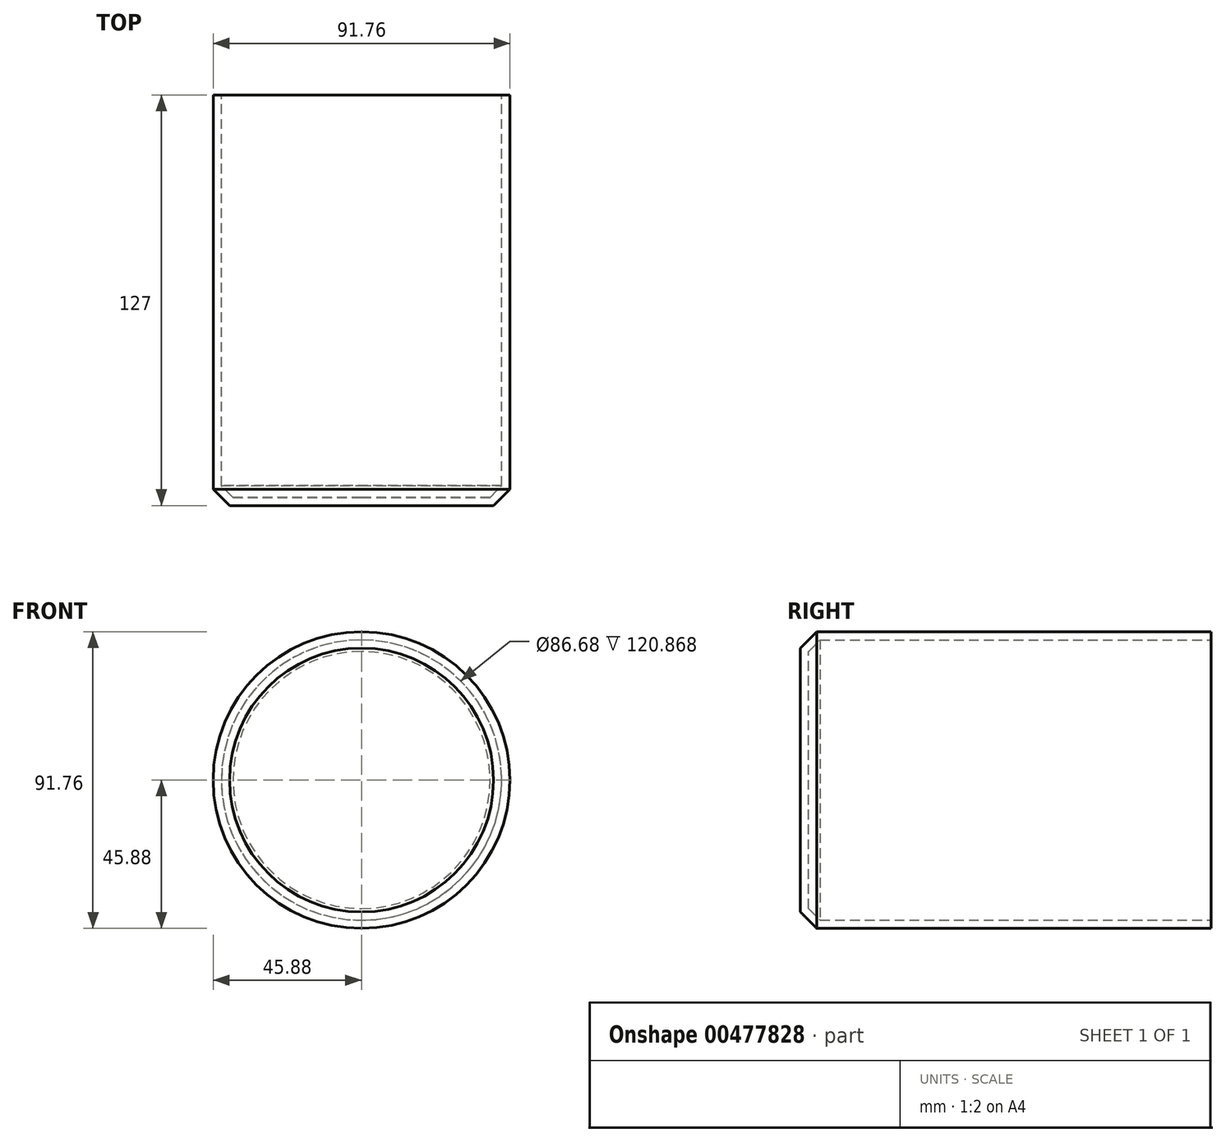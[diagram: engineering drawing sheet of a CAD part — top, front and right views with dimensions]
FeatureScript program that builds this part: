
annotation { "Feature Type Name" : "Feature", "Feature Type Description" : "" }
export const myFeature = defineFeature(function(context is Context, id is Id, definition is map)
    precondition{}
    {
        {
            var Q0;
            Q0=qCreatedBy(makeId("Front.planeOp"),FACE);
            var sketch = newSketch(context, id + "F0", { "sketchPlane" : qUnion([Q0])});
            skCircle(sketch, "E0", {"center": v(0, 0) * mm, "radius": 45.88 * mm});
            skSolve(sketch);
        }
        {
            var Q0;
            Q0 = qSketchRegion(id + "F0", true);
            extrude(context, id + "F1", {"entities" : qUnion([Q0]), "depth" : 127 * mm});
        }
        {
            var Q0;
            Q0=makeQuery(id+"F1.opExtrude","CAP_EDGE",EDGE,{"disambiguationData":[OSD([sQuery(id+"F0.wireOp",EDGE,"E0")])],"isStart":false});
            chamfer(context, id + "F2", {"entities" : qUnion([Q0]), "width" : 5.08 * mm, "tangentPropagation" : true});
        }
        {
            var Q0;
            Q0=makeQuery(id+"F1.opExtrude","CAP_FACE",FACE,{"disambiguationData":[OSD([sQuery(id+"F0.wireOp",EDGE,"E0")])],"isStart":true});
            shell(context, id + "F3", {"entities" : qUnion([Q0]), "thickness" : 2.54 * mm});
        }
    });
